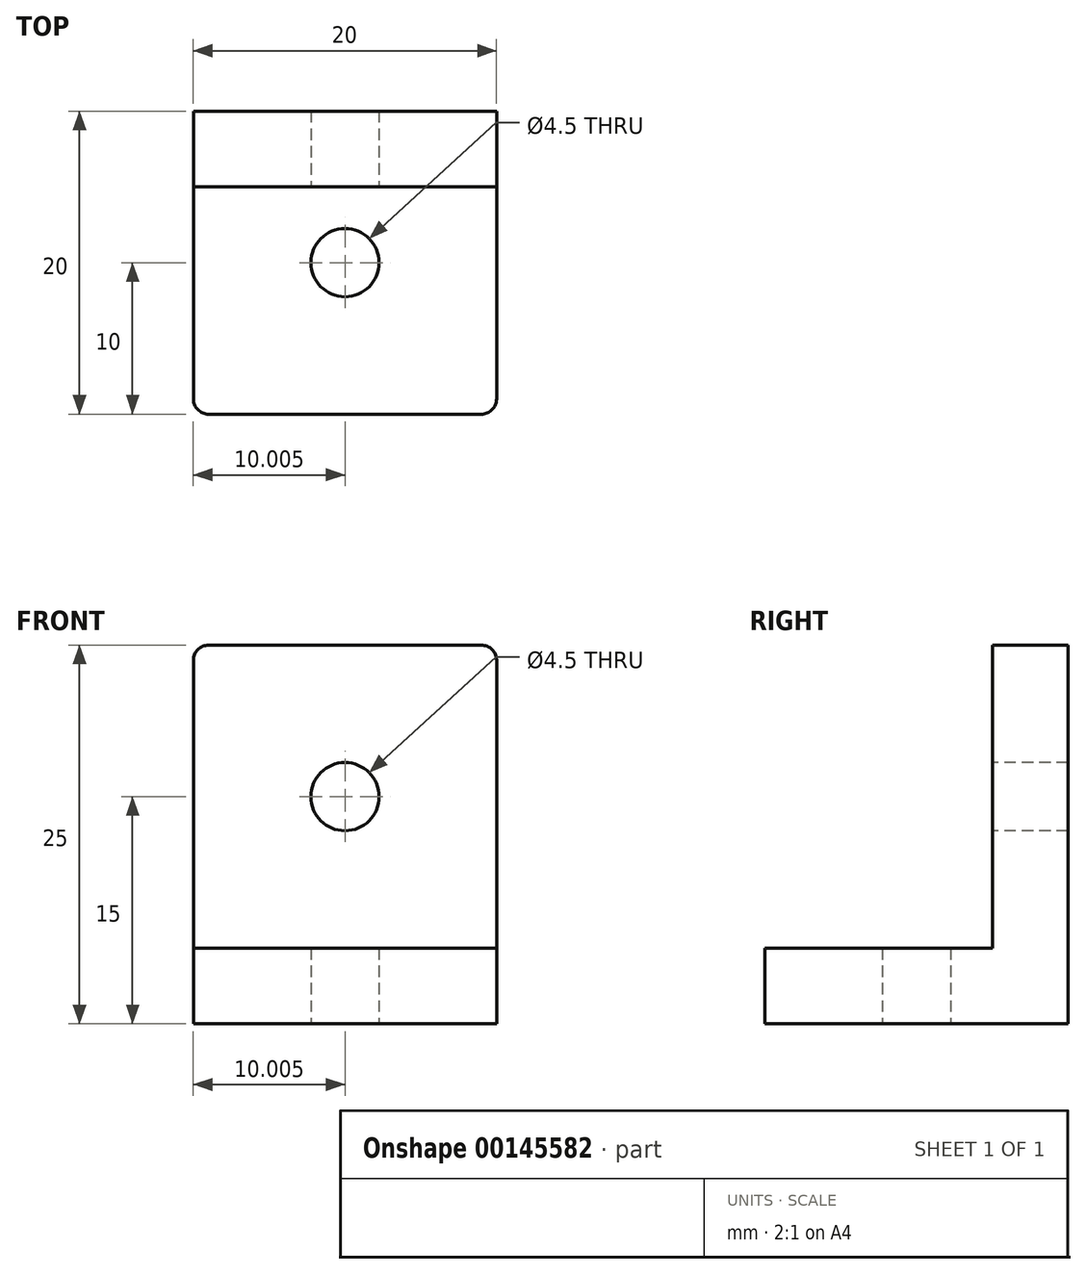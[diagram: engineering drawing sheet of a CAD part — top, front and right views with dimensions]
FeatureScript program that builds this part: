
annotation { "Feature Type Name" : "Feature", "Feature Type Description" : "" }
export const myFeature = defineFeature(function(context is Context, id is Id, definition is map)
    precondition{}
    {
        {
            var Q0;
            Q0=qCreatedBy(makeId("Top.planeOp"),FACE);
            var sketch = newSketch(context, id + "F0", { "sketchPlane" : qUnion([Q0])});
            skLineSegment(sketch, "E0.bottom", {"start": v(-9.66, 0) * mm, "end": v(10.34, 0) * mm});
            skLineSegment(sketch, "E0.top", {"start": v(-9.66, 20) * mm, "end": v(10.34, 20) * mm});
            skLineSegment(sketch, "E0.left", {"start": v(-9.66, 0) * mm, "end": v(-9.66, 20) * mm});
            skLineSegment(sketch, "E0.right", {"start": v(10.34, 0) * mm, "end": v(10.34, 20) * mm});
            skCircle(sketch, "E1", {"center": v(0.34, 10) * mm, "radius": 2.25 * mm});
            skPoint(sketch, "E2", {"position": v(0.34, 20) * mm});
            skPoint(sketch, "E3", {"position": v(-9.66, 10) * mm});
            skLineSegment(sketch, "E4", {"start": v(-9.66, 15) * mm, "end": v(10.34, 15) * mm});
            skSolve(sketch);
        }
        {
            var Q0;
            {var subQ1=sQuery(id+"F0.wireOp",EDGE,"E0.bottom");Q0=makeQuery(id+"F0.imprint","IMPRINT",FACE,{"disambiguationData":[TD([[makeQuery(id+"F0.imprint","IMPRINT",EDGE,{"derivedFrom":subQ1}),1.0]])]});}
            extrude(context, id + "F1", {"entities" : qUnion([Q0]), "offsetDistance" : 25 * mm, "depth" : 5 * mm});
        }
        {
            var Q0;
            {var subQ0=sQuery(id+"F0.wireOp",EDGE,"E0.top");Q0=makeQuery(id+"F0.imprint","IMPRINT",FACE,{"disambiguationData":[TD([[makeQuery(id+"F0.imprint","IMPRINT",EDGE,{"derivedFrom":subQ0}),-1.0]])]});}
            extrude(context, id + "F2", {"entities" : qUnion([Q0]), "operationType" : NewBodyOperationType.ADD, "offsetDistance" : 25 * mm, "depth" : 25 * mm});
        }
        {
            var Q0;
            Q0=makeQuery(id+"F2.opExtrude","SWEPT_FACE",FACE,{"disambiguationData":[OSD([sQuery(id+"F0.wireOp",EDGE,"E4")])]});
            var sketch = newSketch(context, id + "F3", { "sketchPlane" : qUnion([Q0])});
            skPoint(sketch, "E5", {"position": v(0.34, 25) * mm});
            skPoint(sketch, "E6", {"position": v(-9.66, 15) * mm});
            skCircle(sketch, "E7", {"center": v(0.34, 15) * mm, "radius": 2.25 * mm});
            skSolve(sketch);
        }
        {
            var Q0;
            Q0=qSketchRegion(id+"F3",true);
            extrude(context, id + "F4", {"entities" : qUnion([Q0]), "operationType" : NewBodyOperationType.REMOVE, "oppositeDirection" : true, "depth" : 25 * mm});
        }
        {
            var Q0;
            Q0=makeQuery(id+"F2.opExtrude","CAP_EDGE",EDGE,{"disambiguationData":[OSD([sQuery(id+"F0.wireOp",EDGE,"E0.left")])],"isStart":false});
            var Q1;
            Q1=makeQuery(id+"F2.opExtrude","CAP_EDGE",EDGE,{"disambiguationData":[OSD([sQuery(id+"F0.wireOp",EDGE,"E0.right")])],"isStart":false});
            var Q2;
            Q2=makeQuery(id+"F1.opExtrude","SWEPT_EDGE",EDGE,{"disambiguationData":[OSD([sQuery(id+"F0.wireOp",EDGE,"E0.bottom"),sQuery(id+"F0.wireOp",EDGE,"E0.left")])]});
            var Q3;
            Q3=makeQuery(id+"F1.opExtrude","SWEPT_EDGE",EDGE,{"disambiguationData":[OSD([sQuery(id+"F0.wireOp",EDGE,"E0.bottom"),sQuery(id+"F0.wireOp",EDGE,"E0.right")])]});
            var Q4;
            Q4=makeQuery(id+"F1.opExtrude","CAP_EDGE",EDGE,{"disambiguationData":[OSD([sQuery(id+"F0.wireOp",EDGE,"E4")])],"isStart":false});
            fillet(context, id + "F5", {"entities" : qUnion([Q0, Q1, Q2, Q3, Q4]), "radius" : 1 * mm, "tangentPropagation" : true, "allowEdgeOverflow" : false});
        }
    });
